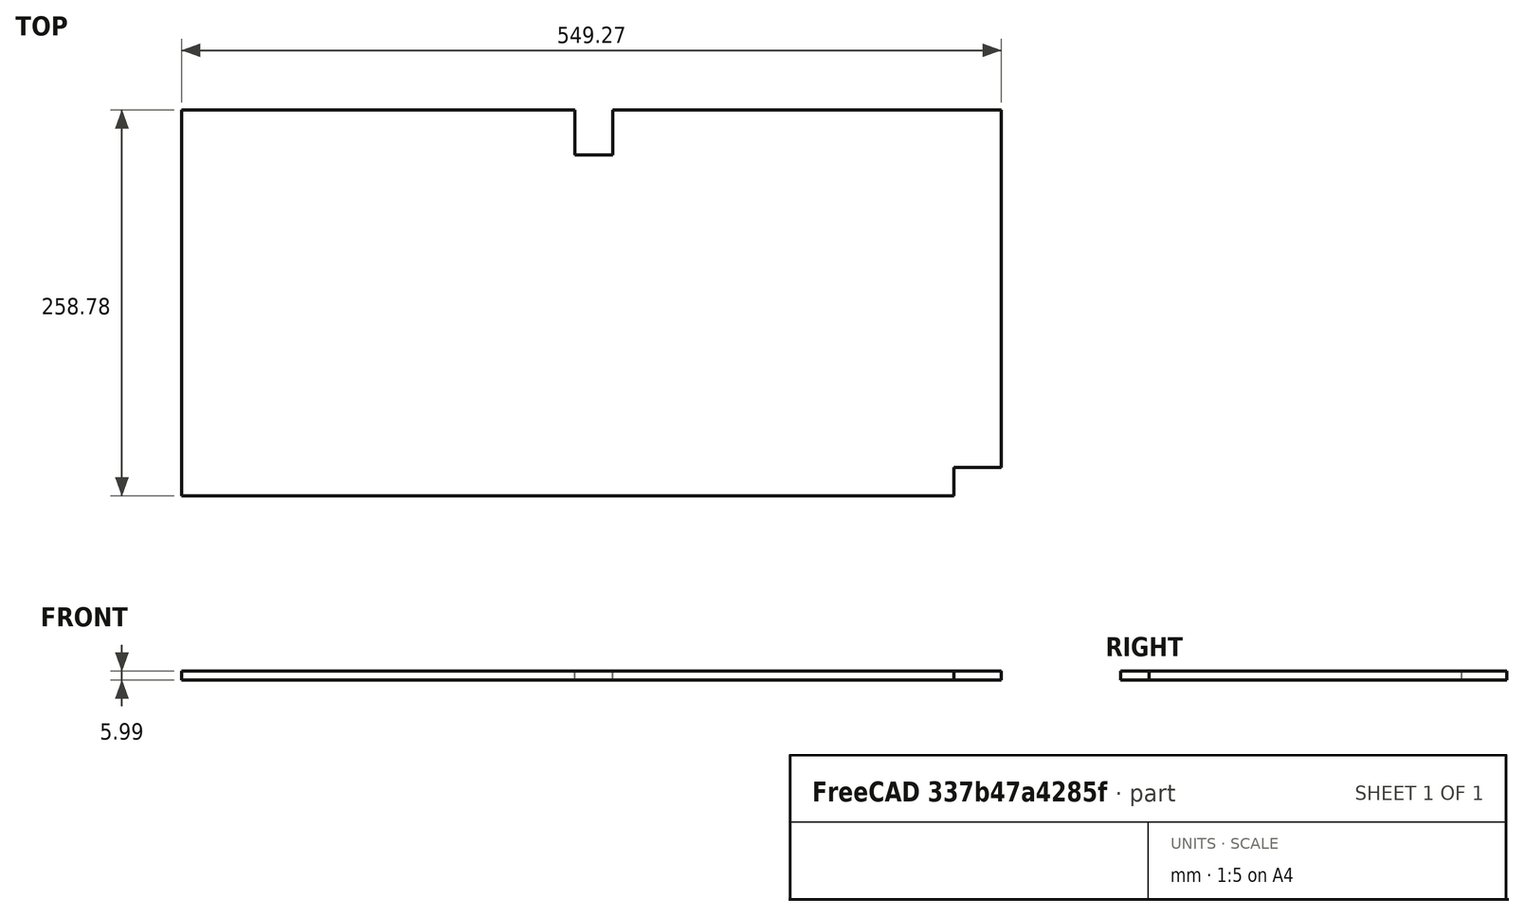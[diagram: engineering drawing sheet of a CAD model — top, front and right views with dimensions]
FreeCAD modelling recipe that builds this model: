
FCSTD DOCUMENT  (FreeCAD 0.19R24267 (Git))
Label: Inv2-P2
License: All rights reserved
LicenseURL: http://en.wikipedia.org/wiki/All_rights_reserved
objects: TechDraw::DrawViewDimension×6, TechDraw::DrawProjGroupItem×2, TechDraw::DrawHatch×2, TechDraw::DrawViewAnnotation×2, Sketcher::SketchObject×1, Part::Extrusion×1, TechDraw::DrawSVGTemplate×1, TechDraw::DrawProjGroup×1, TechDraw::DrawPage×1
note: 2 computed .brp shape members not serialized (recipe doc carries the construction recipe); baked Part::Feature solids carry a one-line shape summary decoded from their .brp

FEATURE [Sketcher::SketchObject] Sketch
  FullyConstrained = true
  sketch-geometry (10):
    g0: LineSegment StartX=0 StartY=7.1e-15 StartZ=0 EndX=263.525 EndY=7.1e-15 EndZ=0
    g1: LineSegment StartX=263.525 StartY=7.1e-15 StartZ=0 EndX=263.525 EndY=-30.1752 EndZ=0
    g2: LineSegment StartX=263.525 StartY=-30.1752 StartZ=0 EndX=288.925 EndY=-30.1752 EndZ=0
    g3: LineSegment StartX=288.925 StartY=-30.1752 StartZ=0 EndX=288.925 EndY=0 EndZ=0
    g4: LineSegment StartX=0 StartY=7.1e-15 StartZ=0 EndX=0 EndY=-258.775 EndZ=0
    g5: LineSegment StartX=0 StartY=-258.775 StartZ=0 EndX=517.525 EndY=-258.775 EndZ=0
    g6: LineSegment StartX=517.525 StartY=-258.775 StartZ=0 EndX=517.525 EndY=-239.725 EndZ=0
    g7: LineSegment StartX=517.525 StartY=-239.725 StartZ=0 EndX=549.275 EndY=-239.725 EndZ=0
    g8: LineSegment StartX=549.275 StartY=-239.725 StartZ=0 EndX=549.275 EndY=0 EndZ=0
    g9: LineSegment StartX=288.925 StartY=0 StartZ=0 EndX=549.275 EndY=0 EndZ=0
  constraints (29):
    c: Horizontal(g0)
    c: DistanceX(g0,g0) = 263.525
    c: Coincident(g1,g0)
    c: Vertical(g1)
    c: DistanceY(g1,g1) = 30.1752
    c: Coincident(g2,g1)
    c: Horizontal(g2)
    c: DistanceX(g2,g2) = 25.4
    c: Coincident(g3,g2)
    c: Vertical(g3)
    c: DistanceY(g3,g3) = 30.1752
    c: Coincident(g4,g0)
    c: Vertical(g4)
    c: DistanceY(g4,g4) = 258.775
    c: Coincident(g5,g4)
    c: Horizontal(g5)
    c: DistanceX(g5,g5) = 517.525
    c: Coincident(g6,g5)
    c: Vertical(g6)
    c: DistanceY(g6,g6) = 19.05
    c: Coincident(g7,g6)
    c: Horizontal(g7)
    c: DistanceX(g7,g7) = 31.75
    c: Coincident(g8,g7)
    c: Vertical(g8)
    c: Coincident(g9,g3)
    c: Coincident(g9,g8)
    c: Coincident(g-1,g0)
    c: Horizontal(g9)
FEATURE [Part::Extrusion] Extrude
  Base = -> Sketch
  Dir = (0,0,1)
  DirMode = 2
  FaceMakerClass = Part::FaceMakerBullseye
  LengthFwd = 5.9944
  LengthRev = 0
  Solid = true
  Symmetric = false
FEATURE [TechDraw::DrawSVGTemplate] Template
  Height = 215.9
  Orientation = 1
  Width = 279.4
FEATURE [TechDraw::DrawProjGroupItem] ProjItem  label="Front"
  CoarseView = false
  Direction = (0,0,1)
  Focus = 100
  HardHidden = false
  IsoCount = 0
  IsoHidden = false
  IsoVisible = false
  LockPosition = true
  Perspective = false
  Rotation = 0
  RotationVector = (1,0,0)
  Scale = 0.2
  ScaleType = 2
  SeamHidden = false
  SeamVisible = true
  SmoothHidden = false
  SmoothVisible = true
  Source = -> [Extrude]
  Type = 0
  X = 0
  XDirection = (1,0,0)
  Y = 0
FEATURE [TechDraw::DrawProjGroupItem] ProjItem001  label="Left"
  CoarseView = false
  Direction = (-1,0,1e-16)
  Focus = 100
  HardHidden = false
  IsoCount = 0
  IsoHidden = false
  IsoVisible = false
  LockPosition = false
  Perspective = false
  Rotation = 0
  RotationVector = (1,0,0)
  Scale = 0.2
  ScaleType = 2
  SeamHidden = false
  SeamVisible = true
  SmoothHidden = false
  SmoothVisible = true
  Source = -> [Extrude]
  Type = 1
  X = 93.901
  XDirection = (1e-16,0,1)
  Y = 0
FEATURE [TechDraw::DrawProjGroup] ProjGroup
  Anchor = -> ProjItem
  AutoDistribute = true
  LockPosition = false
  ProjectionType = 0
  Rotation = 0
  Scale = 0.2
  ScaleType = 2
  Source = -> [Extrude]
  Views = -> [ProjItem,ProjItem001]
  X = 128.041
  Y = 103.034
  spacingX = 15.0114
  spacingY = 15.0114
FEATURE [TechDraw::DrawHatch] Hatch  label="HatchF0"
  HatchPattern = <path>
  Source = -> ProjItem [Face0]
FEATURE [TechDraw::DrawHatch] Hatch001  label="Hatch001F0"
  HatchPattern = <path>
  Source = -> ProjItem001 [Face0]
FEATURE [TechDraw::DrawViewDimension] Dimension
  Arbitrary = false
  ArbitraryTolerances = false
  EqualTolerance = true
  FormatSpec = %.3f
  FormatSpecOverTolerance = %+.3f
  FormatSpecUnderTolerance = %+.3f
  Inverted = false
  LockPosition = false
  MeasureType = 1
  OverTolerance = 0
  References2D = -> [ProjItem]
  Rotation = 0
  ScaleType = 0
  TheoreticalExact = false
  Type = 2
  UnderTolerance = 0
  X = 68.2838
  Y = -2.21777
FEATURE [TechDraw::DrawViewDimension] Dimension001
  Arbitrary = false
  ArbitraryTolerances = false
  EqualTolerance = true
  FormatSpec = %.3f
  FormatSpecOverTolerance = %+.3f
  FormatSpecUnderTolerance = %+.3f
  Inverted = false
  LockPosition = false
  MeasureType = 1
  OverTolerance = 0
  References2D = -> [ProjItem]
  Rotation = 0
  ScaleType = 0
  TheoreticalExact = false
  Type = 1
  UnderTolerance = 0
  X = 34.3976
  Y = -2.60403
FEATURE [TechDraw::DrawViewDimension] Dimension002
  Arbitrary = false
  ArbitraryTolerances = false
  EqualTolerance = true
  FormatSpec = %.3f
  FormatSpecOverTolerance = %+.3f
  FormatSpecUnderTolerance = %+.3f
  Inverted = false
  LockPosition = false
  MeasureType = 1
  OverTolerance = 0
  References2D = -> [ProjItem]
  Rotation = 0
  ScaleType = 0
  TheoreticalExact = false
  Type = 2
  UnderTolerance = 0
  X = 37.5482
  Y = -37.597
FEATURE [TechDraw::DrawViewDimension] Dimension003
  Arbitrary = false
  ArbitraryTolerances = false
  EqualTolerance = true
  FormatSpec = %.3f
  FormatSpecOverTolerance = %+.3f
  FormatSpecUnderTolerance = %+.3f
  Inverted = false
  LockPosition = false
  MeasureType = 1
  OverTolerance = 0
  References2D = -> [ProjItem]
  Rotation = 0
  ScaleType = 0
  TheoreticalExact = false
  Type = 1
  UnderTolerance = 0
  X = 19.5658
  Y = 11.2548
FEATURE [TechDraw::DrawViewDimension] Dimension004
  Arbitrary = false
  ArbitraryTolerances = false
  EqualTolerance = true
  FormatSpec = %.3f
  FormatSpecOverTolerance = %+.3f
  FormatSpecUnderTolerance = %+.3f
  Inverted = false
  LockPosition = false
  MeasureType = 1
  OverTolerance = 0
  References2D = -> [ProjItem]
  Rotation = 0
  ScaleType = 0
  TheoreticalExact = false
  Type = 2
  UnderTolerance = 0
  X = -11.6986
  Y = 35.8896
FEATURE [TechDraw::DrawViewDimension] Dimension005
  Arbitrary = false
  ArbitraryTolerances = false
  EqualTolerance = true
  FormatSpec = %.3f
  FormatSpecOverTolerance = %+.3f
  FormatSpecUnderTolerance = %+.3f
  Inverted = false
  LockPosition = false
  MeasureType = 1
  OverTolerance = 0
  References2D = -> [ProjItem001]
  Rotation = 0
  ScaleType = 0
  TheoreticalExact = false
  Type = 1
  UnderTolerance = 0
  X = 15.0963
  Y = 20.7933
FEATURE [TechDraw::DrawViewAnnotation] Annotation
  Font = osifont
  LineSpace = 80
  LockPosition = false
  MaxWidth = -1
  Rotation = 0
  ScaleType = 0
  Text = Figure S2 (Inverted 2) | Panel 2 [back lower] | Quantity: 1
  TextSize = 5.0038
  TextStyle = 0
  X = 32.6737
  Y = 195.58
FEATURE [TechDraw::DrawViewAnnotation] Annotation002
  Font = osifont
  LineSpace = 80
  LockPosition = false
  MaxWidth = -1
  Rotation = 0
  ScaleType = 0
  Text = Units: Inches
  TextSize = 5.0038
  TextStyle = 0
  X = 259.08
  Y = 5.08
FEATURE [TechDraw::DrawPage] Page
  KeepUpdated = true
  NextBalloonIndex = 1
  ProjectionType = 0
  Template = -> Template
  Views = -> [ProjGroup,Dimension,Dimension001,Dimension002,Dimension003,Dimension004,Dimension005,Annotation,Annotation002]
note: 2 file-system paths scrubbed to <path> (originals preserved in the JSON sidecar)
